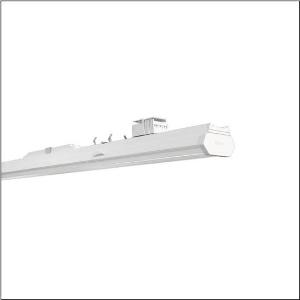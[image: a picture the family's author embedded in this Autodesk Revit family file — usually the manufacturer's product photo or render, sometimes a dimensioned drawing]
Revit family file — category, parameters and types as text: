
# Revit family: licross_r__21_protected_ho_52td12dn4c5l3c_f590
name_source: partatom
category: Lighting Fixtures
units: mm (PartAtom-declared; Revit-internal decimal feet)

## family parameters
Cut with Voids When Loaded = No
Host = Face
Light Source = No
Part Type = Normal
Room Calculation Point = No
Round Connector Dimension = Use Diameter
Shared = No

## types (1)
- --- (1 x LED, 810 lm, 4.8 W, 4000K)
    Apparent Load = 5 VA
    CIE Flux Codes = 70 91 97 98 100
    Color Rendering = 80
    Color Temperature = 4000K
    Default Elevation = 1800 mm
    Description = Licross® 21 Protected HO, luminaire insert, of sheet steel, galvanised, coil coated, white, length: 1.500mm, width: 90mm, height: 103mm, LED rated luminous flux: 12.810lm, light colour: 840, control gear: DALI 2, control gear: ECG DALI, with plug, 6-pole, with phase selection, for trunking rail, 14-core, mains connection: 220..240V, AC, 50/60Hz, rated input power: 83W, halogen-free wiring, for emergency light function, for trunking rail, 14-core, converter,control gear: single battery element, battery: LiFeP04, 9Ah, primary optical cover: cover, of PMMA, light emission: direct distribution, primary light characteristic: symmetric, protection rating (complete): IP54, insulation class (complete): insulation class I (protective earthing), certification: CE, UKCA, protection symbol: D if used in an environment with non-conductive dust loads with corresponding accessories, impact resistance: IK06, permissible ambient temperature for indoor applications: +5..+30°C, standard: EN 60598-2-22, corresponds to IFS (International Featured Standards) requirements for safety and quality in the food industry, reducing of maximum allowable ambient temperature of 5°C with ceiling mounting, LABS conformity tested according to VDMA 24364:2018-05, packaging unit: 1 piece
    Height = 92 mm
    Lamp = 1 x LED
    Lamp Light Flux = 810 lm
    Lamp Power = 4.8 W
    Lamp count = 1
    Length = 1500 mm
    Luminous efficacy = 169 lm/W
    Manufacturer = Siteco
    ModVariant = No
    Model = 52TD12DN4C5L3C
    Mounting Place = Ceiling
    Mounting Type = Pendant
    Number of Poles = 1
    OnlyDefault = Yes
    Power Factor = 1
    Product Name = Licross® 21 Protected HO
    Product group = luminaire insert
    ProductGroupID = 901
    Protection Class = Protection class I
    Protection Degree = IP 54
    RLX_Detail_Level = 1
    RLX_Emergency_Light_Flux = 0 lm
    RLX_Emergency_Type = 0
    RLX_Emergency_Type_DB = No
    RlxData = <blob elided: 24785 chars, md5=9074effb>
    Socket = socket
    Standby Power = 0 W
    System Light Flux = 810 lm
    System Power = 5 W
    Type Comments = : emergency light operation: 3 h
    Type Image = l_1256148.jpg
    URL = http://relux.com
    VarID = @adj_133955
    Voltage = 0 V
    Weight = 0.00 kg
    Width = 88 mm

## geometry (parser evidence)
native form markers: Blend x4, Sweep x10
no freeform markers — native parametric forms only
